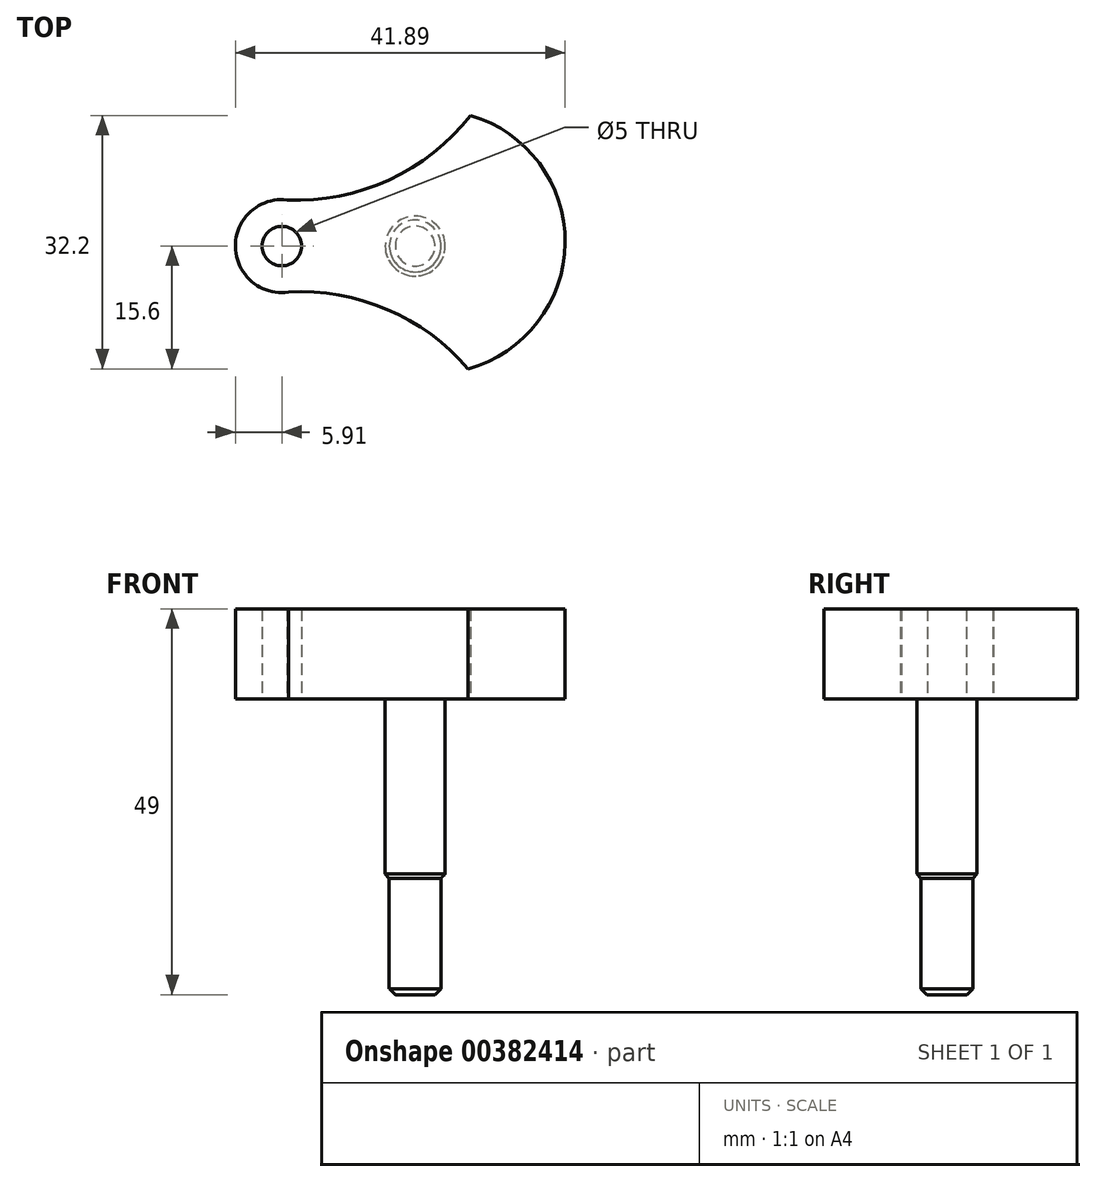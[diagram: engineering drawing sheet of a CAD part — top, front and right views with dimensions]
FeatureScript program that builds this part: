
annotation { "Feature Type Name" : "Feature", "Feature Type Description" : "" }
export const myFeature = defineFeature(function(context is Context, id is Id, definition is map)
    precondition{}
    {
        {
            var Q0;
            Q0=qCreatedBy(makeId("Top.planeOp"),FACE);
            var sketch = newSketch(context, id + "F0", { "sketchPlane" : qUnion([Q0])});
            skCircle(sketch, "E0", {"center": v(0, 0) * mm, "radius": 5.9 * mm});
            skCircle(sketch, "E1", {"center": v(0, 0) * mm, "radius": 2.5 * mm});
            skArc(sketch, "E2", {"start": v(23.66, -15.6) * mm, "mid": v(13, -7.9) * mm, "end": v(0, -5.9) * mm});
            skArc(sketch, "E3", {"start": v(0, 5.9) * mm, "mid": v(13.32, 8.27) * mm, "end": v(23.98, 16.6) * mm});
            skArc(sketch, "E4", {"start": v(23.66, -15.6) * mm, "mid": v(35.98, 0.38) * mm, "end": v(23.98, 16.6) * mm});
            skSolve(sketch);
        }
        {
            var Q0;
            {var subQ5=sQuery(id+"F0.wireOp",EDGE,"E4");Q0=makeQuery(id+"F0.imprint","IMPRINT",FACE,{"disambiguationData":[TD([[makeQuery(id+"F0.imprint","IMPRINT",EDGE,{"derivedFrom":subQ5}),1.0]])]});}
            var Q1;
            Q1=makeQuery(id+"F0.imprint","IMPRINT",FACE,{"disambiguationData":[TD([[makeQuery(id+"F0.imprint","IMPRINT",EDGE,{"derivedFrom":sQuery(id+"F0.wireOp",EDGE,"E1")}),-1.0]])]});
            var Q2;
            {var subQ0=sQuery(id+"F0.wireOp",EDGE,"E3");var subQ1=sQuery(id+"F0.wireOp",EDGE,"E0");var subQ2=makeQuery(id+"F0.imprint","INTERSECT",VERTEX,{"disambiguationData":[OD(0.0)],"derivedFrom":[subQ1,subQ0]});Q2=makeQuery(id+"F0.imprint","IMPRINT",FACE,{"disambiguationData":[TD([[makeQuery(id+"F0.imprint","IMPRINT",EDGE,{"disambiguationData":[TD([[subQ2,1.0]])],"derivedFrom":subQ1}),1.0]])]});}
            var Q3;
            {var subQ0=sQuery(id+"F0.wireOp",EDGE,"E2");var subQ1=sQuery(id+"F0.wireOp",EDGE,"E0");var subQ2=makeQuery(id+"F0.imprint","INTERSECT",VERTEX,{"disambiguationData":[OD(0.0)],"derivedFrom":[subQ1,subQ0]});Q3=makeQuery(id+"F0.imprint","IMPRINT",FACE,{"disambiguationData":[TD([[makeQuery(id+"F0.imprint","IMPRINT",EDGE,{"disambiguationData":[TD([[subQ2,-1.0]])],"derivedFrom":subQ1}),1.0]])]});}
            extrude(context, id + "F1", {"entities" : qUnion([Q0, Q1, Q2, Q3]), "depth" : 11.43 * mm});
        }
        {
            var Q0;
            Q0=makeQuery(id+"F1.opExtrude","CAP_FACE",FACE,{"disambiguationData":[OSD([sQuery(id+"F0.wireOp",EDGE,"E0"),sQuery(id+"F0.wireOp",EDGE,"E2"),sQuery(id+"F0.wireOp",EDGE,"E3"),sQuery(id+"F0.wireOp",EDGE,"E4")])],"isStart":true});
            var sketch = newSketch(context, id + "F2", { "sketchPlane" : qUnion([Q0])});
            skCircle(sketch, "E5", {"center": v(16.94, 0) * mm, "radius": 3.81 * mm});
            skSolve(sketch);
        }
        {
            var Q0;
            Q0 = qSketchRegion(id + "F2", true);
            extrude(context, id + "F3", {"entities" : qUnion([Q0]), "operationType" : NewBodyOperationType.ADD, "depth" : 23.01 * mm});
        }
        {
            var Q0;
            Q0=makeQuery(id+"F3.opExtrude","CAP_FACE",FACE,{"disambiguationData":[OSD([sQuery(id+"F2.wireOp",EDGE,"E5")])],"isStart":false});
            var sketch = newSketch(context, id + "F4", { "sketchPlane" : qUnion([Q0])});
            skCircle(sketch, "E6", {"center": v(16.94, 0) * mm, "radius": 3.29 * mm});
            skSolve(sketch);
        }
        {
            var Q0;
            Q0 = qSketchRegion(id + "F4", true);
            extrude(context, id + "F5", {"entities" : qUnion([Q0]), "operationType" : NewBodyOperationType.ADD, "depth" : 14.55 * mm});
        }
        {
            var Q0;
            Q0=makeQuery(id+"F3.opExtrude","CAP_EDGE",EDGE,{"disambiguationData":[OSD([sQuery(id+"F2.wireOp",EDGE,"E5")])],"isStart":false});
            chamfer(context, id + "F6", {"entities" : qUnion([Q0]), "width" : 0.76 * mm, "tangentPropagation" : true});
        }
        {
            var Q0;
            Q0=makeQuery(id+"F5.opExtrude","CAP_EDGE",EDGE,{"disambiguationData":[OSD([sQuery(id+"F4.wireOp",EDGE,"E6")])],"isStart":false});
            chamfer(context, id + "F7", {"entities" : qUnion([Q0]), "width" : 0.76 * mm, "tangentPropagation" : true});
        }
    });
